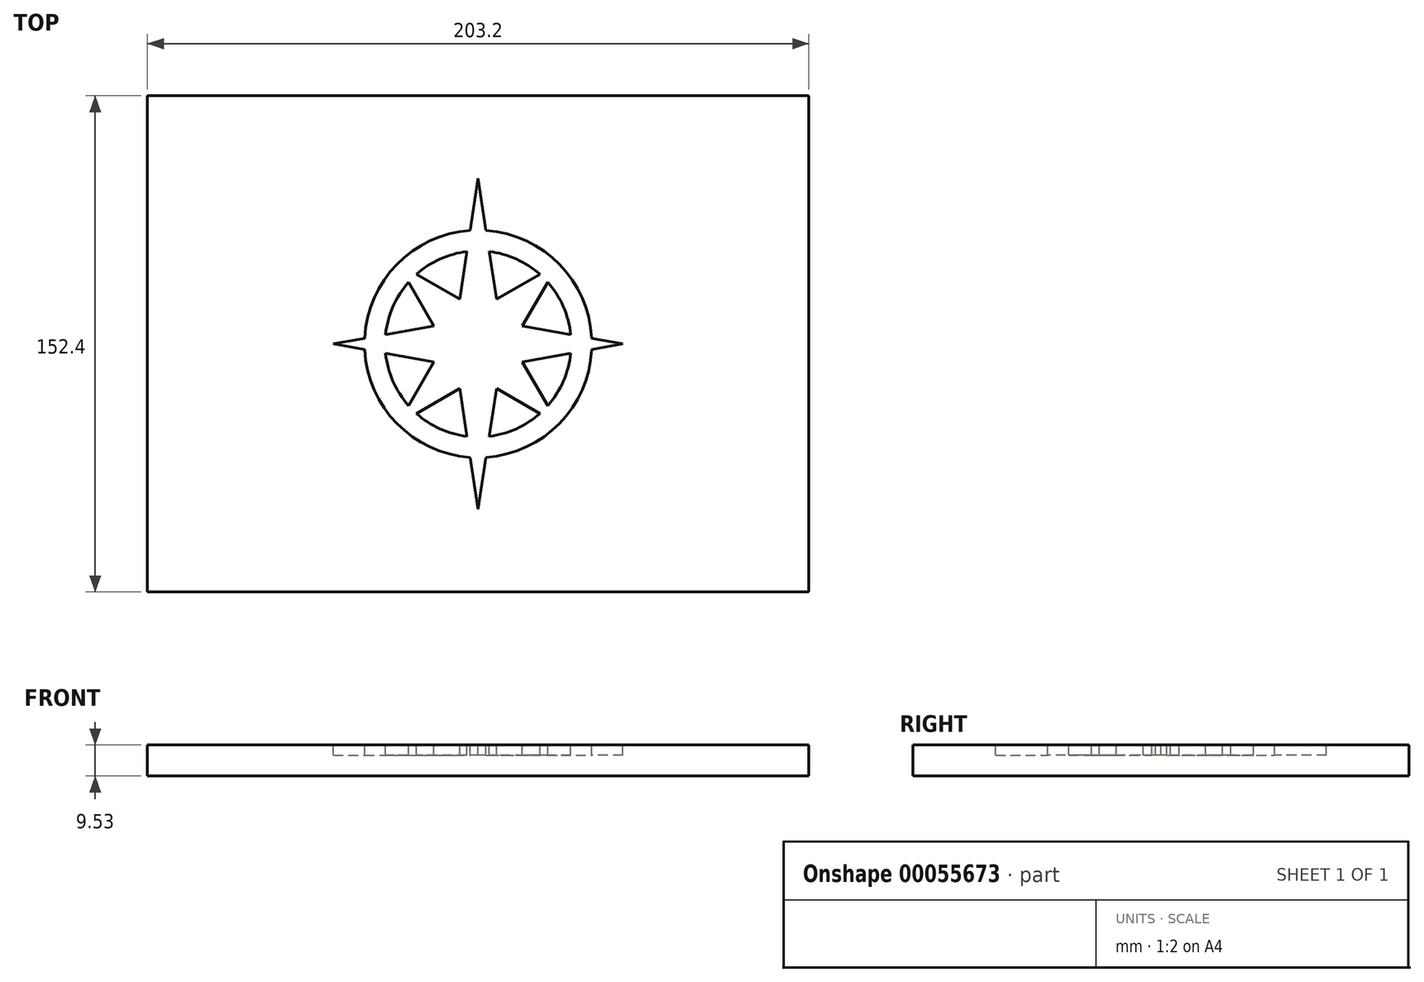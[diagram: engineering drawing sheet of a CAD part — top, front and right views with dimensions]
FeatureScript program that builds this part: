
annotation { "Feature Type Name" : "Feature", "Feature Type Description" : "" }
export const myFeature = defineFeature(function(context is Context, id is Id, definition is map)
    precondition{}
    {
        {
            var Q0;
            Q0=qCreatedBy(makeId("Top.planeOp"),FACE);
            var sketch = newSketch(context, id + "F0", { "sketchPlane" : qUnion([Q0])});
            skLineSegment(sketch, "E0.rect.bottom", {"start": v(-101.6, 76.2) * mm, "end": v(101.6, 76.2) * mm});
            skLineSegment(sketch, "E0.rect.top", {"start": v(-101.6, -76.2) * mm, "end": v(101.6, -76.2) * mm});
            skLineSegment(sketch, "E0.rect.left", {"start": v(-101.6, 76.2) * mm, "end": v(-101.6, -76.2) * mm});
            skLineSegment(sketch, "E0.rect.right", {"start": v(101.6, 76.2) * mm, "end": v(101.6, -76.2) * mm});
            skPoint(sketch, "E0.rect.middle", {"position": v(0, 0) * mm});
            skSolve(sketch);
        }
        {
            var Q0;
            Q0 = qSketchRegion(id + "F0", true);
            extrude(context, id + "F1", {"entities" : qUnion([Q0]), "oppositeDirection" : true, "depth" : 9.52 * mm});
        }
        {
            var Q0;
            Q0=qCreatedBy(makeId("Top.planeOp"),FACE);
            var sketch = newSketch(context, id + "F2", { "sketchPlane" : qUnion([Q0])});
            skCircle(sketch, "E1", {"center": v(0, 0) * mm, "radius": 50.8 * mm});
            skCircle(sketch, "E2", {"center": v(0, 0) * mm, "radius": 44.45 * mm});
            skCircle(sketch, "E3", {"center": v(0, 0) * mm, "radius": 34.93 * mm});
            skCircle(sketch, "E4", {"center": v(0, 0) * mm, "radius": 9.53 * mm});
            skLineSegment(sketch, "E5.bottom", {"start": v(-6.74, -6.74) * mm, "end": v(6.74, -6.74) * mm});
            skLineSegment(sketch, "E5.top", {"start": v(-6.74, 6.74) * mm, "end": v(6.74, 6.74) * mm});
            skLineSegment(sketch, "E5.left", {"start": v(-6.74, -6.74) * mm, "end": v(-6.74, 6.74) * mm});
            skLineSegment(sketch, "E5.right", {"start": v(6.74, -6.74) * mm, "end": v(6.74, 6.74) * mm});
            skSolve(sketch);
        }
        {
            var Q0;
            Q0=qCreatedBy(makeId("Top.planeOp"),FACE);
            var sketch = newSketch(context, id + "F3", { "sketchPlane" : qUnion([Q0])});
            skLineSegment(sketch, "E6", {"start": v(0, 50.8) * mm, "end": v(0, -50.8) * mm});
            skLineSegment(sketch, "E7", {"start": v(-44.45, 0) * mm, "end": v(44.45, 0) * mm});
            skLineSegment(sketch, "E8", {"start": v(0, -50.8) * mm, "end": v(-6.74, -6.74) * mm});
            skLineSegment(sketch, "E9", {"start": v(-6.74, -6.74) * mm, "end": v(-44.45, 0) * mm});
            skLineSegment(sketch, "E10", {"start": v(-44.45, 0) * mm, "end": v(-6.74, 6.74) * mm});
            skLineSegment(sketch, "E11", {"start": v(-6.74, 6.74) * mm, "end": v(0, 50.8) * mm});
            skLineSegment(sketch, "E12", {"start": v(0, 50.8) * mm, "end": v(6.74, 6.74) * mm});
            skLineSegment(sketch, "E13", {"start": v(6.74, 6.74) * mm, "end": v(44.45, 0) * mm});
            skLineSegment(sketch, "E14", {"start": v(44.45, 0) * mm, "end": v(6.74, -6.74) * mm});
            skLineSegment(sketch, "E15", {"start": v(6.74, -6.74) * mm, "end": v(0, -50.8) * mm});
            skLineSegment(sketch, "E16", {"start": v(-6.74, -6.74) * mm, "end": v(6.74, 6.74) * mm});
            skLineSegment(sketch, "E17", {"start": v(-6.74, 6.74) * mm, "end": v(6.74, -6.74) * mm});
            skLineSegment(sketch, "E18", {"start": v(6.74, 6.74) * mm, "end": v(24.7, 24.7) * mm});
            skLineSegment(sketch, "E19", {"start": v(6.74, -6.74) * mm, "end": v(24.7, -24.7) * mm});
            skLineSegment(sketch, "E20", {"start": v(-6.74, -6.74) * mm, "end": v(-24.7, -24.7) * mm});
            skLineSegment(sketch, "E21", {"start": v(-6.74, 6.74) * mm, "end": v(-24.7, 24.7) * mm});
            skLineSegment(sketch, "E22", {"start": v(-24.7, 24.7) * mm, "end": v(-13.62, 5.5) * mm});
            skLineSegment(sketch, "E23", {"start": v(-24.7, 24.7) * mm, "end": v(-5.67, 13.71) * mm});
            skLineSegment(sketch, "E24", {"start": v(24.7, 24.7) * mm, "end": v(5.67, 13.71) * mm});
            skLineSegment(sketch, "E25", {"start": v(24.7, 24.7) * mm, "end": v(13.62, 5.5) * mm});
            skLineSegment(sketch, "E26", {"start": v(24.7, -24.7) * mm, "end": v(5.67, -13.71) * mm});
            skLineSegment(sketch, "E27", {"start": v(24.7, -24.7) * mm, "end": v(13.62, -5.5) * mm});
            skLineSegment(sketch, "E28", {"start": v(-24.7, -24.7) * mm, "end": v(-5.67, -13.71) * mm});
            skLineSegment(sketch, "E29", {"start": v(-24.7, -24.7) * mm, "end": v(-13.62, -5.5) * mm});
            skArc(sketch, "E30", {"start": v(-34.88, -1.7) * mm, "mid": v(-24.95, -24.44) * mm, "end": v(-2.44, -34.84) * mm});
            skArc(sketch, "E31", {"start": v(-18.96, -21.38) * mm, "mid": v(-11.72, -26.06) * mm, "end": v(-3.43, -28.37) * mm});
            skArc(sketch, "E32.trimOffspring", {"start": v(-28.43, -2.86) * mm, "mid": v(-26.17, -11.46) * mm, "end": v(-21.38, -18.96) * mm});
            skArc(sketch, "E33.trimOffspring", {"start": v(-21.38, 18.96) * mm, "mid": v(-26.17, 11.46) * mm, "end": v(-28.43, 2.86) * mm});
            skArc(sketch, "E34.trimOffspring", {"start": v(-3.43, 28.37) * mm, "mid": v(-11.72, 26.06) * mm, "end": v(-18.96, 21.38) * mm});
            skArc(sketch, "E35.trimOffspring", {"start": v(18.96, 21.38) * mm, "mid": v(11.72, 26.06) * mm, "end": v(3.43, 28.37) * mm});
            skArc(sketch, "E36.trimOffspring", {"start": v(28.43, 2.86) * mm, "mid": v(26.17, 11.46) * mm, "end": v(21.38, 18.96) * mm});
            skArc(sketch, "E37.trimOffspring", {"start": v(34.88, 1.7) * mm, "mid": v(24.95, 24.44) * mm, "end": v(2.44, 34.84) * mm});
            skArc(sketch, "E38.trimOffspring", {"start": v(21.38, -18.96) * mm, "mid": v(26.17, -11.46) * mm, "end": v(28.43, -2.86) * mm});
            skArc(sketch, "E39.trimOffspring", {"start": v(2.44, -34.84) * mm, "mid": v(24.95, -24.44) * mm, "end": v(34.88, -1.7) * mm});
            skArc(sketch, "E40.trimOffspring", {"start": v(3.43, -28.37) * mm, "mid": v(11.72, -26.06) * mm, "end": v(18.96, -21.38) * mm});
            skArc(sketch, "E41.trimOffspring", {"start": v(-2.44, 34.84) * mm, "mid": v(-24.95, 24.44) * mm, "end": v(-34.88, 1.7) * mm});
            skSolve(sketch);
        }
        {
            var Q0;
            Q0 = qSketchRegion(id + "F3", true);
            extrude(context, id + "F4", {"entities" : qUnion([Q0]), "operationType" : NewBodyOperationType.REMOVE, "oppositeDirection" : true, "depth" : 3.17 * mm});
        }
    });
